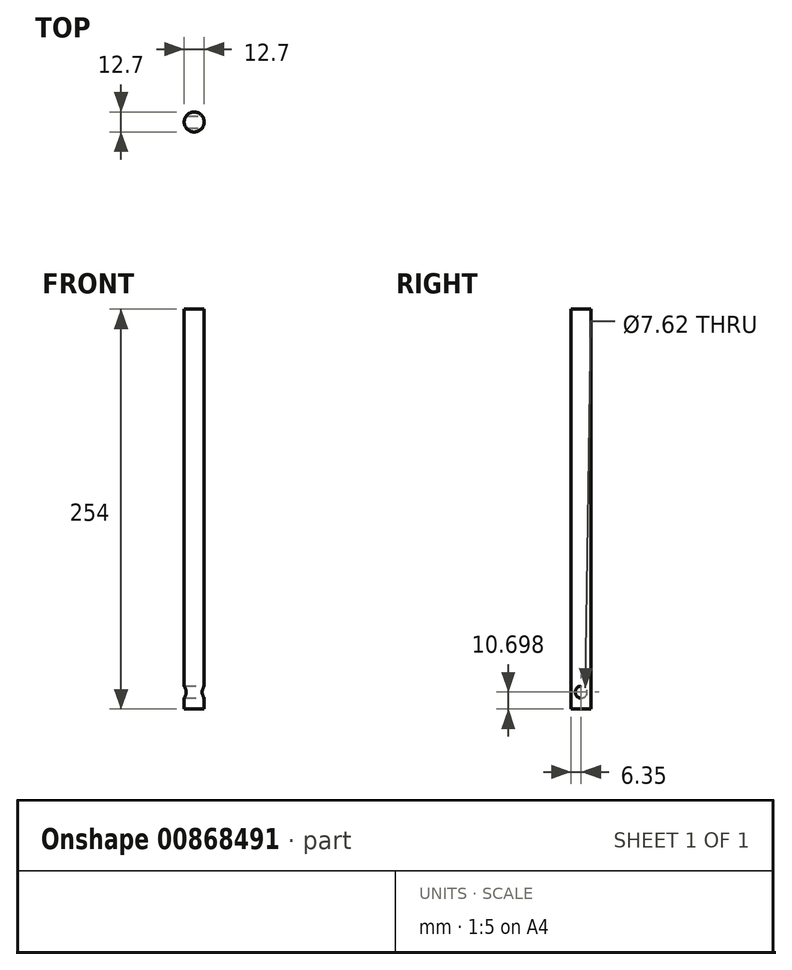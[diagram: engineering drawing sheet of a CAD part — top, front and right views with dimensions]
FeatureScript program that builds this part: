
annotation { "Feature Type Name" : "Feature", "Feature Type Description" : "" }
export const myFeature = defineFeature(function(context is Context, id is Id, definition is map)
    precondition{}
    {
        {
            var Q0;
            Q0=qCreatedBy(makeId("Top.planeOp"),FACE);
            var sketch = newSketch(context, id + "F0", { "sketchPlane" : qUnion([Q0])});
            skCircle(sketch, "E0", {"center": v(0, 0) * mm, "radius": 6.35 * mm});
            skSolve(sketch);
        }
        {
            var Q0;
            Q0 = qSketchRegion(id + "F0", true);
            extrude(context, id + "F1", {"entities" : qUnion([Q0]), "depth" : 254 * mm, "offsetDistance" : 25.4 * mm});
        }
        {
            var Q0;
            Q0=qCreatedBy(makeId("Right.planeOp"),FACE);
            var sketch = newSketch(context, id + "F2", { "sketchPlane" : qUnion([Q0])});
            skLineSegment(sketch, "E1", {"start": v(0, -125.86) * mm, "end": v(0, 140.1) * mm, "construction": true});
            skCircle(sketch, "E2", {"center": v(0, 10.7) * mm, "radius": 3.81 * mm});
            skSolve(sketch);
        }
        {
            var Q0;
            Q0 = qSketchRegion(id + "F2", true);
            extrude(context, id + "F3", {"entities" : qUnion([Q0]), "operationType" : NewBodyOperationType.REMOVE, "endBound" : BoundingType.SYMMETRIC, "oppositeDirection" : true, "depth" : 25.4 * mm, "offsetDistance" : 25.4 * mm});
        }
    });
